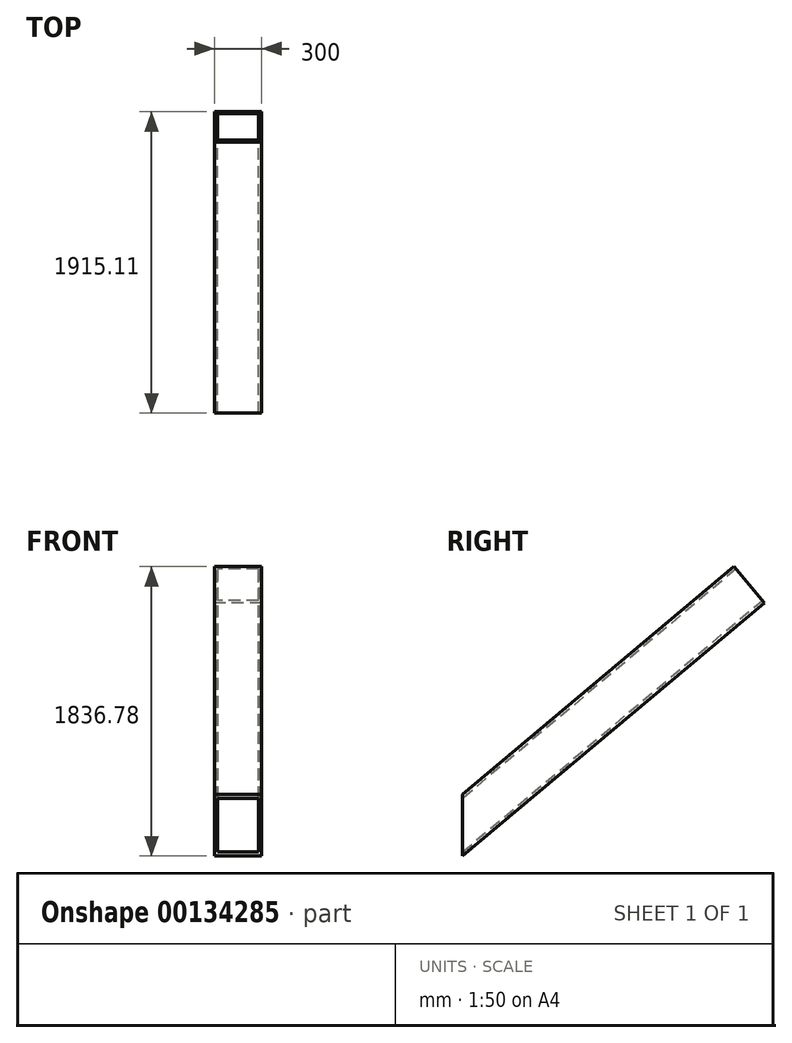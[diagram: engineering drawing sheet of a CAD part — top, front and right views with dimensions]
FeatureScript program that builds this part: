
annotation { "Feature Type Name" : "Feature", "Feature Type Description" : "" }
export const myFeature = defineFeature(function(context is Context, id is Id, definition is map)
    precondition{}
    {
        {
            var Q0;
            Q0=qCreatedBy(makeId("Right.planeOp"),FACE);
            var sketch = newSketch(context, id + "F0", { "sketchPlane" : qUnion([Q0])});
            skLineSegment(sketch, "E0", {"start": v(0, 0) * mm, "end": v(1915.11, 1606.97) * mm});
            skLineSegment(sketch, "E1", {"start": v(1915.11, 1606.97) * mm, "end": v(1722.27, 1836.78) * mm});
            skLineSegment(sketch, "E2", {"start": v(1722.27, 1836.78) * mm, "end": v(0, 391.62) * mm});
            skLineSegment(sketch, "E3", {"start": v(0, 391.62) * mm, "end": v(0, 0) * mm});
            skSolve(sketch);
        }
        {
            var Q0;
            Q0 = qSketchRegion(id + "F0", true);
            extrude(context, id + "F1", {"entities" : qUnion([Q0]), "depth" : 300 * mm});
        }
        {
            var Q0;
            Q0=makeQuery(id+"F1.opExtrude","SWEPT_FACE",FACE,{"disambiguationData":[OSD([sQuery(id+"F0.wireOp",EDGE,"E3")])]});
            var Q1;
            Q1=makeQuery(id+"F1.opExtrude","SWEPT_FACE",FACE,{"disambiguationData":[OSD([sQuery(id+"F0.wireOp",EDGE,"E1")])]});
            shell(context, id + "F2", {"entities" : qUnion([Q0, Q1]), "thickness" : 20 * mm});
        }
    });
